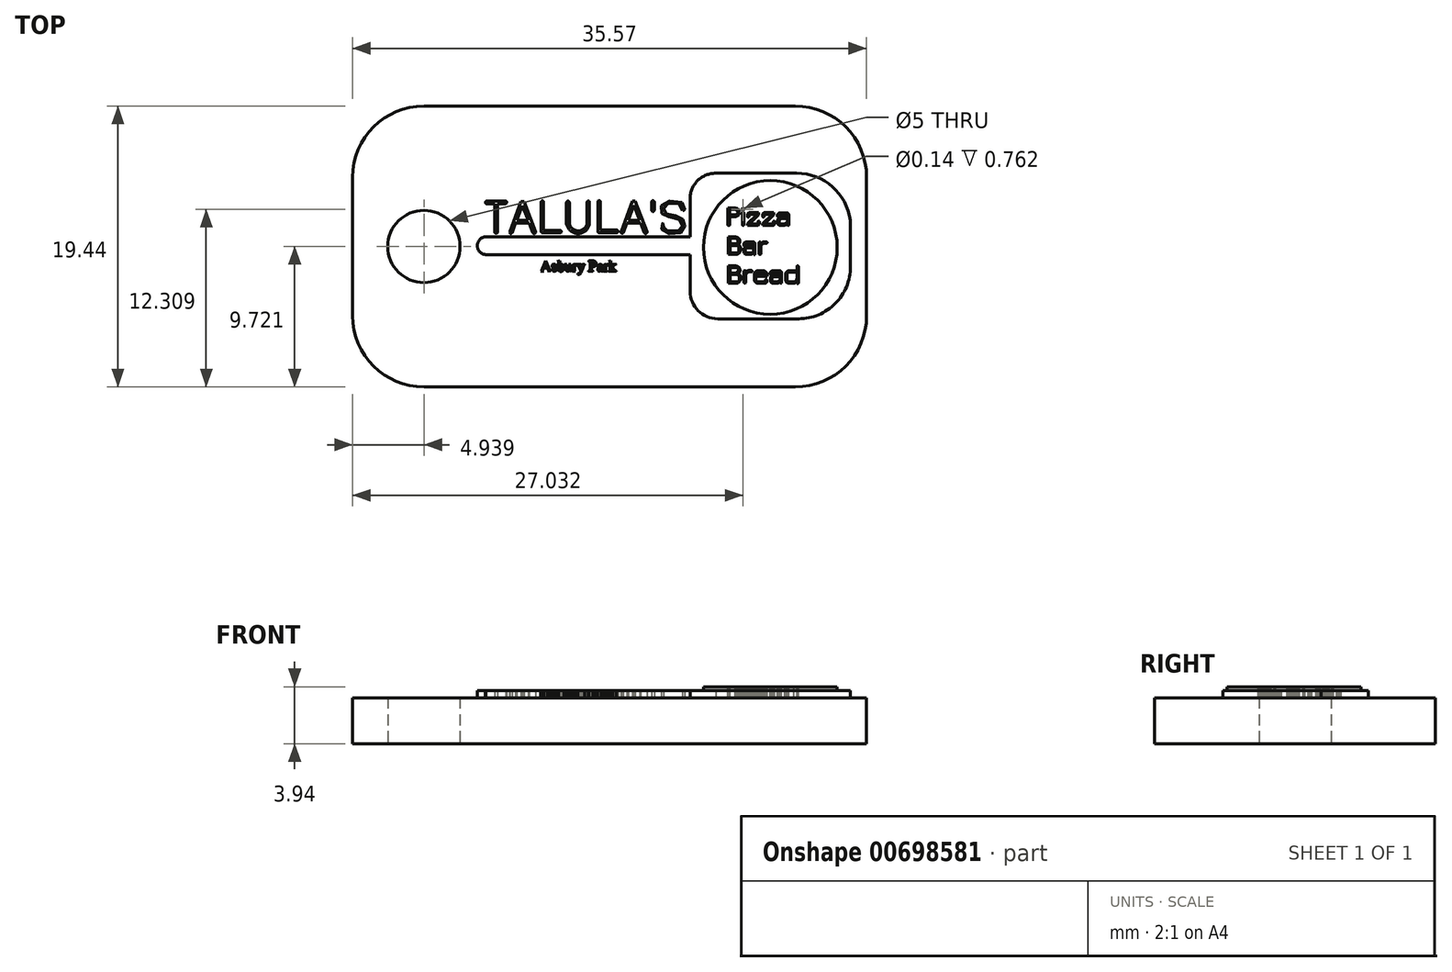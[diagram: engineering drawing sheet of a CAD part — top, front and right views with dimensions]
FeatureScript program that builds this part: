
annotation { "Feature Type Name" : "Feature", "Feature Type Description" : "" }
export const myFeature = defineFeature(function(context is Context, id is Id, definition is map)
    precondition{}
    {
        {
            var Q0;
            Q0=qCreatedBy(makeId("Top.planeOp"),FACE);
            var sketch = newSketch(context, id + "F0", { "sketchPlane" : qUnion([Q0])});
            skLineSegment(sketch, "E0.bottom", {"start": v(-4.93, 0) * mm, "end": v(-30.63, 0) * mm});
            skLineSegment(sketch, "E0.top", {"start": v(-4.93, 19.44) * mm, "end": v(-30.63, 19.44) * mm});
            skLineSegment(sketch, "E0.left", {"start": v(0, 4.93) * mm, "end": v(0, 14.5) * mm});
            skLineSegment(sketch, "E0.right", {"start": v(-35.57, 4.93) * mm, "end": v(-35.57, 14.5) * mm});
            skPoint(sketch, "E1.visualSharp", {"position": v(-35.57, 0) * mm});
            skArc(sketch, "E1.filletArc", {"start": v(-35.57, 4.93) * mm, "mid": v(-34.12, 1.45) * mm, "end": v(-30.63, 0) * mm});
            skPoint(sketch, "E2.visualSharp", {"position": v(-35.57, 19.44) * mm});
            skArc(sketch, "E2.filletArc", {"start": v(-30.63, 19.44) * mm, "mid": v(-34.12, 18) * mm, "end": v(-35.57, 14.5) * mm});
            skPoint(sketch, "E3.visualSharp", {"position": v(0, 19.44) * mm});
            skArc(sketch, "E3.filletArc", {"start": v(0, 14.5) * mm, "mid": v(-1.45, 18) * mm, "end": v(-4.93, 19.44) * mm});
            skPoint(sketch, "E4.visualSharp", {"position": v(0, 0) * mm});
            skArc(sketch, "E4.filletArc", {"start": v(-4.93, 0) * mm, "mid": v(-1.45, 1.45) * mm, "end": v(0, 4.93) * mm});
            skCircle(sketch, "E5", {"center": v(-30.63, 9.72) * mm, "radius": 2.5 * mm});
            skPoint(sketch, "E5.centerSnap0", {"position": v(-35.57, 9.72) * mm});
            skSolve(sketch);
        }
        {
            var Q0;
            Q0 = qSketchRegion(id + "F0", true);
            extrude(context, id + "F1", {"entities" : qUnion([Q0]), "depth" : 3.17 * mm, "offsetDistance" : 25.4 * mm});
        }
        {
            var Q0;
            Q0=makeQuery(id+"F1.opExtrude","CAP_FACE",FACE,{"disambiguationData":[OSD([sQuery(id+"F0.wireOp",EDGE,"E0.bottom"),sQuery(id+"F0.wireOp",EDGE,"E0.top"),sQuery(id+"F0.wireOp",EDGE,"E0.left"),sQuery(id+"F0.wireOp",EDGE,"E0.right"),sQuery(id+"F0.wireOp",EDGE,"E1.filletArc"),sQuery(id+"F0.wireOp",EDGE,"E2.filletArc"),sQuery(id+"F0.wireOp",EDGE,"E3.filletArc"),sQuery(id+"F0.wireOp",EDGE,"E4.filletArc"),sQuery(id+"F0.wireOp",EDGE,"E5")])],"isStart":false});
            var sketch = newSketch(context, id + "F2", { "sketchPlane" : qUnion([Q0])});
            skLineSegment(sketch, "E6", {"start": v(-26.47, 10.38) * mm, "end": v(-12.21, 10.38) * mm});
            skLineSegment(sketch, "E7", {"start": v(-12.21, 10.38) * mm, "end": v(-12.21, 13.03) * mm});
            skLineSegment(sketch, "E8", {"start": v(-10.42, 14.8) * mm, "end": v(-4.84, 14.8) * mm});
            skLineSegment(sketch, "E9", {"start": v(-1.12, 11.52) * mm, "end": v(-1.12, 8.32) * mm});
            skLineSegment(sketch, "E10", {"start": v(-10.3, 4.72) * mm, "end": v(-4.7, 4.72) * mm});
            skLineSegment(sketch, "E11", {"start": v(-26.37, 9.16) * mm, "end": v(-12.21, 9.16) * mm});
            skLineSegment(sketch, "E12", {"start": v(-12.21, 9.16) * mm, "end": v(-12.21, 6.63) * mm});
            skArc(sketch, "E13", {"start": v(-10.42, 14.8) * mm, "mid": v(-11.69, 14.28) * mm, "end": v(-12.21, 13.03) * mm});
            skArc(sketch, "E14", {"start": v(-1.12, 11.52) * mm, "mid": v(-2.37, 13.86) * mm, "end": v(-4.84, 14.8) * mm});
            skArc(sketch, "E15", {"start": v(-4.7, 4.72) * mm, "mid": v(-2.16, 5.78) * mm, "end": v(-1.12, 8.32) * mm});
            skArc(sketch, "E16", {"start": v(-12.21, 6.63) * mm, "mid": v(-11.65, 5.28) * mm, "end": v(-10.3, 4.72) * mm});
            skArc(sketch, "E17", {"start": v(-26.47, 10.38) * mm, "mid": v(-26.94, 9.73) * mm, "end": v(-26.37, 9.16) * mm});
            skLineSegment(sketch, "E18", {"start": v(-26.3, 12.86) * mm, "end": v(-24.96, 12.86) * mm});
            skLineSegment(sketch, "E19", {"start": v(-26.3, 12.69) * mm, "end": v(-25.72, 12.69) * mm});
            skLineSegment(sketch, "E20", {"start": v(-25.72, 12.69) * mm, "end": v(-25.72, 10.7) * mm});
            skLineSegment(sketch, "E21", {"start": v(-25.53, 10.7) * mm, "end": v(-25.53, 12.69) * mm});
            skLineSegment(sketch, "E22", {"start": v(-25.53, 12.69) * mm, "end": v(-24.96, 12.69) * mm});
            skArc(sketch, "E23", {"start": v(-24.96, 12.69) * mm, "mid": v(-24.9, 12.78) * mm, "end": v(-24.96, 12.86) * mm});
            skArc(sketch, "E24", {"start": v(-26.3, 12.86) * mm, "mid": v(-26.38, 12.78) * mm, "end": v(-26.3, 12.69) * mm});
            skArc(sketch, "E25", {"start": v(-25.72, 10.7) * mm, "mid": v(-25.63, 10.63) * mm, "end": v(-25.53, 10.7) * mm});
            skLineSegment(sketch, "E26", {"start": v(-24.69, 10.75) * mm, "end": v(-23.92, 12.85) * mm});
            skLineSegment(sketch, "E27", {"start": v(-23.92, 12.85) * mm, "end": v(-23.7, 12.85) * mm});
            skLineSegment(sketch, "E28", {"start": v(-23.7, 12.85) * mm, "end": v(-22.9, 10.74) * mm});
            skLineSegment(sketch, "E29", {"start": v(-24.2, 11.53) * mm, "end": v(-23.82, 12.56) * mm});
            skLineSegment(sketch, "E30", {"start": v(-23.82, 12.56) * mm, "end": v(-23.4, 11.53) * mm});
            skLineSegment(sketch, "E31", {"start": v(-23.4, 11.53) * mm, "end": v(-24.2, 11.53) * mm});
            skLineSegment(sketch, "E32", {"start": v(-24.53, 10.68) * mm, "end": v(-24.3, 11.34) * mm});
            skLineSegment(sketch, "E33", {"start": v(-24.3, 11.34) * mm, "end": v(-23.35, 11.34) * mm});
            skLineSegment(sketch, "E34", {"start": v(-23.35, 11.34) * mm, "end": v(-23.1, 10.68) * mm});
            skArc(sketch, "E35", {"start": v(-24.69, 10.75) * mm, "mid": v(-24.65, 10.63) * mm, "end": v(-24.53, 10.68) * mm});
            skArc(sketch, "E36", {"start": v(-23.1, 10.68) * mm, "mid": v(-22.97, 10.62) * mm, "end": v(-22.9, 10.74) * mm});
            skLineSegment(sketch, "E37", {"start": v(-22.5, 12.84) * mm, "end": v(-22.5, 10.75) * mm});
            skLineSegment(sketch, "E38", {"start": v(-22.36, 12.84) * mm, "end": v(-22.36, 10.84) * mm});
            skLineSegment(sketch, "E39", {"start": v(-22.36, 10.84) * mm, "end": v(-21.2, 10.84) * mm});
            skLineSegment(sketch, "E40", {"start": v(-22.44, 10.66) * mm, "end": v(-21.2, 10.66) * mm});
            skArc(sketch, "E41", {"start": v(-22.36, 12.84) * mm, "mid": v(-22.43, 12.88) * mm, "end": v(-22.5, 12.84) * mm});
            skArc(sketch, "E42", {"start": v(-22.5, 10.75) * mm, "mid": v(-22.49, 10.7) * mm, "end": v(-22.44, 10.66) * mm});
            skArc(sketch, "E43", {"start": v(-21.2, 10.66) * mm, "mid": v(-21.12, 10.75) * mm, "end": v(-21.2, 10.84) * mm});
            skLineSegment(sketch, "E44", {"start": v(-18.59, 12.86) * mm, "end": v(-18.59, 10.77) * mm});
            skLineSegment(sketch, "E45", {"start": v(-18.44, 12.86) * mm, "end": v(-18.44, 10.86) * mm});
            skLineSegment(sketch, "E46", {"start": v(-18.44, 10.86) * mm, "end": v(-17.29, 10.86) * mm});
            skLineSegment(sketch, "E47", {"start": v(-18.52, 10.68) * mm, "end": v(-17.28, 10.68) * mm});
            skArc(sketch, "E48", {"start": v(-18.44, 12.86) * mm, "mid": v(-18.51, 12.9) * mm, "end": v(-18.59, 12.86) * mm});
            skArc(sketch, "E49", {"start": v(-18.59, 10.77) * mm, "mid": v(-18.57, 10.72) * mm, "end": v(-18.52, 10.68) * mm});
            skArc(sketch, "E50", {"start": v(-17.28, 10.68) * mm, "mid": v(-17.2, 10.77) * mm, "end": v(-17.29, 10.86) * mm});
            skLineSegment(sketch, "E51", {"start": v(-16.98, 10.76) * mm, "end": v(-16.2, 12.86) * mm});
            skLineSegment(sketch, "E52", {"start": v(-16.2, 12.86) * mm, "end": v(-16, 12.86) * mm});
            skLineSegment(sketch, "E53", {"start": v(-16, 12.86) * mm, "end": v(-15.2, 10.74) * mm});
            skLineSegment(sketch, "E54", {"start": v(-16.5, 11.54) * mm, "end": v(-16.1, 12.57) * mm});
            skLineSegment(sketch, "E55", {"start": v(-16.1, 12.57) * mm, "end": v(-15.7, 11.54) * mm});
            skLineSegment(sketch, "E56", {"start": v(-15.7, 11.54) * mm, "end": v(-16.5, 11.54) * mm});
            skLineSegment(sketch, "E57", {"start": v(-16.82, 10.69) * mm, "end": v(-16.58, 11.34) * mm});
            skLineSegment(sketch, "E58", {"start": v(-16.58, 11.34) * mm, "end": v(-15.64, 11.34) * mm});
            skLineSegment(sketch, "E59", {"start": v(-15.64, 11.34) * mm, "end": v(-15.39, 10.68) * mm});
            skArc(sketch, "E60", {"start": v(-16.98, 10.76) * mm, "mid": v(-16.94, 10.64) * mm, "end": v(-16.82, 10.69) * mm});
            skArc(sketch, "E61", {"start": v(-15.39, 10.68) * mm, "mid": v(-15.26, 10.63) * mm, "end": v(-15.2, 10.74) * mm});
            skArc(sketch, "E62", {"start": v(-20.57, 11.3) * mm, "mid": v(-19.95, 10.8) * mm, "end": v(-19.34, 11.3) * mm});
            skArc(sketch, "E63", {"start": v(-20.76, 11.28) * mm, "mid": v(-19.96, 10.62) * mm, "end": v(-19.17, 11.3) * mm});
            skLineSegment(sketch, "E64", {"start": v(-20.76, 11.28) * mm, "end": v(-20.76, 12.77) * mm});
            skLineSegment(sketch, "E65", {"start": v(-20.57, 11.3) * mm, "end": v(-20.57, 12.77) * mm});
            skLineSegment(sketch, "E66", {"start": v(-19.34, 11.3) * mm, "end": v(-19.34, 12.77) * mm});
            skLineSegment(sketch, "E67", {"start": v(-19.17, 11.3) * mm, "end": v(-19.17, 12.79) * mm});
            skArc(sketch, "E68", {"start": v(-20.57, 12.77) * mm, "mid": v(-20.67, 12.87) * mm, "end": v(-20.76, 12.77) * mm});
            skArc(sketch, "E69", {"start": v(-19.17, 12.79) * mm, "mid": v(-19.26, 12.87) * mm, "end": v(-19.34, 12.77) * mm});
            skLineSegment(sketch, "E70", {"start": v(-14.86, 12.22) * mm, "end": v(-14.86, 12.81) * mm});
            skLineSegment(sketch, "E71", {"start": v(-14.7, 12.22) * mm, "end": v(-14.7, 12.83) * mm});
            skArc(sketch, "E72", {"start": v(-14.7, 12.83) * mm, "mid": v(-14.79, 12.9) * mm, "end": v(-14.86, 12.81) * mm});
            skArc(sketch, "E73", {"start": v(-14.86, 12.22) * mm, "mid": v(-14.78, 12.14) * mm, "end": v(-14.7, 12.22) * mm});
            skFitSpline(sketch, "E74", {"points": [v(-12.75, 12.2) * mm, v(-12.78, 12.43) * mm, v(-12.8, 12.53) * mm, v(-12.91, 12.63) * mm, v(-13.07, 12.7) * mm, v(-13.36, 12.72) * mm, v(-13.78, 12.71) * mm, v(-13.9, 12.64) * mm, v(-14, 12.53) * mm, v(-14.03, 12.43) * mm, v(-14.04, 12.22) * mm, v(-14, 12.12) * mm, v(-13.98, 12.07) * mm, v(-13.92, 12.01) * mm, v(-13.84, 11.98) * mm, v(-13.78, 11.96) * mm, v(-13.58, 11.92) * mm, v(-13.16, 11.83) * mm, v(-12.97, 11.79) * mm, v(-12.84, 11.72) * mm, v(-12.73, 11.62) * mm, v(-12.66, 11.52) * mm, v(-12.62, 11.44) * mm, v(-12.6, 11.38) * mm, v(-12.58, 11.16) * mm, v(-12.61, 10.99) * mm, v(-12.7, 10.82) * mm, v(-12.81, 10.72) * mm, v(-12.99, 10.64) * mm, v(-13.35, 10.62) * mm, v(-13.76, 10.63) * mm, v(-13.93, 10.69) * mm, v(-14.12, 10.83) * mm, v(-14.18, 10.98) * mm, v(-14.2, 11.14) * mm, v(-14.2, 11.31) * mm, v(-14.14, 11.34) * mm, v(-14.1, 11.34) * mm, v(-14.08, 11.33) * mm, v(-14.07, 11.3) * mm, v(-14.06, 11.25) * mm, v(-14.06, 11.17) * mm, v(-14.05, 11.08) * mm, v(-14.04, 11.01) * mm, v(-14.02, 10.97) * mm, v(-13.98, 10.92) * mm, v(-13.95, 10.87) * mm, v(-13.88, 10.84) * mm, v(-13.78, 10.83) * mm, v(-13.32, 10.8) * mm, v(-13.03, 10.81) * mm, v(-12.88, 10.88) * mm, v(-12.84, 10.94) * mm, v(-12.78, 11.04) * mm, v(-12.76, 11.15) * mm, v(-12.77, 11.35) * mm, v(-12.82, 11.47) * mm, v(-12.9, 11.55) * mm, v(-13.06, 11.62) * mm, v(-13.3, 11.67) * mm, v(-13.7, 11.77) * mm, v(-13.95, 11.83) * mm, v(-14.05, 11.87) * mm, v(-14.15, 11.98) * mm, v(-14.17, 12.03) * mm, v(-14.2, 12.07) * mm, v(-14.2, 12.17) * mm, v(-14.2, 12.43) * mm, v(-14.13, 12.65) * mm, v(-13.94, 12.83) * mm, v(-13.71, 12.86) * mm, v(-13.04, 12.86) * mm, v(-12.82, 12.8) * mm, v(-12.71, 12.72) * mm, v(-12.64, 12.6) * mm, v(-12.6, 12.48) * mm, v(-12.58, 12.28) * mm, v(-12.59, 12.24) * mm, v(-12.61, 12.17) * mm, v(-12.63, 12.16) * mm, v(-12.67, 12.16) * mm, v(-12.72, 12.16) * mm, v(-12.75, 12.2) * mm]});
            skPoint(sketch, "E75.1.internal.orphan", {"position": v(-13.07, 12.73) * mm});
            skCircle(sketch, "E76", {"center": v(-6.66, 9.66) * mm, "radius": 4.63 * mm});
            skPoint(sketch, "E76.perimeterSnap0", {"position": v(-6.66, 9.66) * mm});
            skPoint(sketch, "E76.perimeterSnap1", {"position": v(-11.69, 14.28) * mm});
            skLineSegment(sketch, "E77", {"start": v(-22.48, 8.07) * mm, "end": v(-22.2, 8.73) * mm});
            skLineSegment(sketch, "E78", {"start": v(-22.2, 8.73) * mm, "end": v(-21.92, 8.07) * mm});
            skLineSegment(sketch, "E79", {"start": v(-22.48, 8.07) * mm, "end": v(-22.5, 8.04) * mm});
            skLineSegment(sketch, "E80", {"start": v(-22.5, 8.04) * mm, "end": v(-22.54, 8.02) * mm});
            skLineSegment(sketch, "E81", {"start": v(-22.54, 8.02) * mm, "end": v(-22.34, 8.02) * mm});
            skLineSegment(sketch, "E82", {"start": v(-22.34, 8.02) * mm, "end": v(-22.38, 8.03) * mm});
            skLineSegment(sketch, "E83", {"start": v(-22.38, 8.03) * mm, "end": v(-22.43, 8.06) * mm});
            skLineSegment(sketch, "E84", {"start": v(-22.43, 8.06) * mm, "end": v(-22.35, 8.23) * mm});
            skLineSegment(sketch, "E85", {"start": v(-22.35, 8.23) * mm, "end": v(-22.07, 8.23) * mm});
            skLineSegment(sketch, "E86", {"start": v(-22.07, 8.23) * mm, "end": v(-22, 8.07) * mm});
            skLineSegment(sketch, "E87", {"start": v(-22, 8.07) * mm, "end": v(-22.04, 8.04) * mm});
            skLineSegment(sketch, "E88", {"start": v(-22.04, 8.04) * mm, "end": v(-22.09, 8.03) * mm});
            skLineSegment(sketch, "E89", {"start": v(-22.09, 8.03) * mm, "end": v(-21.84, 8.03) * mm});
            skLineSegment(sketch, "E90", {"start": v(-21.84, 8.03) * mm, "end": v(-21.92, 8.07) * mm});
            skLineSegment(sketch, "E91", {"start": v(-22.21, 8.56) * mm, "end": v(-22.34, 8.26) * mm});
            skLineSegment(sketch, "E92", {"start": v(-22.34, 8.26) * mm, "end": v(-22.1, 8.26) * mm});
            skLineSegment(sketch, "E93", {"start": v(-22.1, 8.26) * mm, "end": v(-22.21, 8.56) * mm});
            skLineSegment(sketch, "E94", {"start": v(-21.4, 8.69) * mm, "end": v(-21.24, 8.75) * mm});
            skLineSegment(sketch, "E95", {"start": v(-21.24, 8.75) * mm, "end": v(-21.24, 8.43) * mm});
            skLineSegment(sketch, "E96", {"start": v(-21.4, 8.69) * mm, "end": v(-21.33, 8.69) * mm});
            skLineSegment(sketch, "E97", {"start": v(-21.33, 8.69) * mm, "end": v(-21.33, 8.07) * mm});
            skLineSegment(sketch, "E98", {"start": v(-21.23, 8.38) * mm, "end": v(-21.23, 8.08) * mm});
            skLineSegment(sketch, "E99", {"start": v(-21, 8.35) * mm, "end": v(-21, 8.16) * mm});
            skLineSegment(sketch, "E100", {"start": v(-20.92, 8.35) * mm, "end": v(-20.92, 8.18) * mm});
            skLineSegment(sketch, "E101", {"start": v(-20.74, 8.12) * mm, "end": v(-20.74, 8.48) * mm});
            skLineSegment(sketch, "E102", {"start": v(-20.74, 8.48) * mm, "end": v(-20.9, 8.48) * mm});
            skLineSegment(sketch, "E103", {"start": v(-20.9, 8.48) * mm, "end": v(-20.87, 8.46) * mm});
            skLineSegment(sketch, "E104", {"start": v(-20.87, 8.46) * mm, "end": v(-20.8, 8.46) * mm});
            skLineSegment(sketch, "E105", {"start": v(-20.8, 8.46) * mm, "end": v(-20.8, 8.1) * mm});
            skLineSegment(sketch, "E106", {"start": v(-20.72, 8.01) * mm, "end": v(-20.65, 8.01) * mm});
            skLineSegment(sketch, "E107", {"start": v(-20.52, 8.08) * mm, "end": v(-20.52, 8) * mm});
            skLineSegment(sketch, "E108", {"start": v(-20.52, 8) * mm, "end": v(-20.4, 8.08) * mm});
            skLineSegment(sketch, "E109", {"start": v(-20.4, 8.08) * mm, "end": v(-20.45, 8.08) * mm});
            skLineSegment(sketch, "E110", {"start": v(-20.45, 8.08) * mm, "end": v(-20.45, 8.5) * mm});
            skLineSegment(sketch, "E111", {"start": v(-20.45, 8.5) * mm, "end": v(-20.6, 8.5) * mm});
            skLineSegment(sketch, "E112", {"start": v(-20.6, 8.5) * mm, "end": v(-20.6, 8.46) * mm});
            skLineSegment(sketch, "E113", {"start": v(-20.6, 8.46) * mm, "end": v(-20.53, 8.46) * mm});
            skLineSegment(sketch, "E114", {"start": v(-20.53, 8.46) * mm, "end": v(-20.53, 8.13) * mm});
            skLineSegment(sketch, "E115", {"start": v(-21.47, 8.48) * mm, "end": v(-21.47, 8.36) * mm});
            skLineSegment(sketch, "E116", {"start": v(-21.76, 8.16) * mm, "end": v(-21.76, 8) * mm});
            skLineSegment(sketch, "E117", {"start": v(-21.64, 8) * mm, "end": v(-21.57, 8) * mm});
            skLineSegment(sketch, "E118", {"start": v(-20.36, 8.42) * mm, "end": v(-20.3, 8.42) * mm});
            skLineSegment(sketch, "E119", {"start": v(-20.3, 8.42) * mm, "end": v(-20.3, 8.06) * mm});
            skLineSegment(sketch, "E120", {"start": v(-20.2, 8.5) * mm, "end": v(-20.2, 8.44) * mm});
            skLineSegment(sketch, "E121", {"start": v(-20.2, 8.39) * mm, "end": v(-20.2, 8.07) * mm});
            skLineSegment(sketch, "E122", {"start": v(-20.35, 8.01) * mm, "end": v(-20.13, 8.01) * mm});
            skLineSegment(sketch, "E123", {"start": v(-20.02, 8.5) * mm, "end": v(-19.82, 8.5) * mm});
            skLineSegment(sketch, "E124", {"start": v(-19.65, 8.5) * mm, "end": v(-19.5, 8.5) * mm});
            skLineSegment(sketch, "E125", {"start": v(-19.97, 8.46) * mm, "end": v(-19.77, 8.03) * mm});
            skLineSegment(sketch, "E126", {"start": v(-19.87, 8.41) * mm, "end": v(-19.74, 8.13) * mm});
            skLineSegment(sketch, "E127", {"start": v(-19.74, 8.13) * mm, "end": v(-19.61, 8.42) * mm});
            skPoint(sketch, "E128.10.internal.snap0", {"position": v(-21.62, 8.5) * mm});
            skFitSpline(sketch, "E128", {"points": [v(-21.47, 8.48) * mm, v(-21.51, 8.47) * mm, v(-21.55, 8.48) * mm, v(-21.58, 8.5) * mm, v(-21.65, 8.5) * mm, v(-21.7, 8.48) * mm, v(-21.75, 8.43) * mm, v(-21.77, 8.37) * mm, v(-21.76, 8.32) * mm, v(-21.73, 8.28) * mm, v(-21.62, 8.2) * mm, v(-21.54, 8.17) * mm, v(-21.52, 8.14) * mm, v(-21.52, 8.1) * mm, v(-21.56, 8.05) * mm, v(-21.63, 8.04) * mm, v(-21.68, 8.08) * mm, v(-21.73, 8.15) * mm, v(-21.76, 8.16) * mm], "startDerivative": vector(-0.78, -0.39) * mm, "endDerivative": vector(-0.74, 0.12) * mm});
            skFitSpline(sketch, "E129", {"points": [v(-21.76, 8) * mm, v(-21.72, 8.04) * mm, v(-21.68, 8.02) * mm, v(-21.64, 8) * mm, v(-21.57, 8) * mm, v(-21.5, 8.02) * mm, v(-21.45, 8.08) * mm, v(-21.43, 8.14) * mm, v(-21.47, 8.22) * mm, v(-21.58, 8.3) * mm, v(-21.64, 8.32) * mm, v(-21.69, 8.36) * mm, v(-21.7, 8.42) * mm, v(-21.63, 8.46) * mm, v(-21.56, 8.44) * mm, v(-21.52, 8.4) * mm, v(-21.51, 8.36) * mm, v(-21.47, 8.33) * mm, v(-21.47, 8.36) * mm], "startDerivative": vector(0.84, 1.07) * mm, "endDerivative": vector(-0.22, 0.9) * mm});
            skFitSpline(sketch, "E130", {"points": [v(-21.23, 8.08) * mm, v(-21.15, 8.04) * mm, v(-21.05, 8.08) * mm, v(-21, 8.16) * mm], "startDerivative": vector(0.25, -0.16) * mm, "endDerivative": vector(0.1, 0.3) * mm});
            skFitSpline(sketch, "E131", {"points": [v(-21.23, 8.38) * mm, v(-21.15, 8.44) * mm, v(-21.07, 8.43) * mm, v(-21, 8.35) * mm], "startDerivative": vector(0.25, 0.21) * mm, "endDerivative": vector(0.16, -0.27) * mm});
            skFitSpline(sketch, "E132", {"points": [v(-21.24, 8.43) * mm, v(-21.15, 8.5) * mm, v(-21.04, 8.48) * mm, v(-20.92, 8.35) * mm], "startDerivative": vector(0.26, 0.25) * mm, "endDerivative": vector(0.26, -0.43) * mm});
            skFitSpline(sketch, "E133", {"points": [v(-20.92, 8.18) * mm, v(-21, 8.06) * mm, v(-21.12, 8) * mm, v(-21.23, 8) * mm, v(-21.33, 8.07) * mm], "startDerivative": vector(-0.22, -0.47) * mm, "endDerivative": vector(-0.4, 0.33) * mm});
            skFitSpline(sketch, "E134", {"points": [v(-20.74, 8.12) * mm, v(-20.67, 8.05) * mm, v(-20.53, 8.13) * mm], "startDerivative": vector(0.12, -0.21) * mm, "endDerivative": vector(0.29, 0.22) * mm});
            skFitSpline(sketch, "E135", {"points": [v(-20.8, 8.1) * mm, v(-20.77, 8.04) * mm, v(-20.72, 8.01) * mm], "startDerivative": vector(0.03, -0.16) * mm, "endDerivative": vector(0.13, -0.04) * mm});
            skFitSpline(sketch, "E136", {"points": [v(-20.65, 8.01) * mm, v(-20.59, 8.03) * mm, v(-20.52, 8.08) * mm], "startDerivative": vector(0.13, 0.04) * mm, "endDerivative": vector(0.14, 0.1) * mm});
            skFitSpline(sketch, "E137", {"points": [v(-20.36, 8.42) * mm, v(-20.31, 8.46) * mm, v(-20.2, 8.5) * mm], "startDerivative": vector(0.1, 0.1) * mm, "endDerivative": vector(0.22, 0.05) * mm});
            skFitSpline(sketch, "E138", {"points": [v(-20.3, 8.06) * mm, v(-20.3, 8.04) * mm, v(-20.32, 8.03) * mm, v(-20.35, 8.01) * mm], "startDerivative": vector(-0.05, -0.08) * mm, "endDerivative": vector(-0.08, -0.05) * mm});
            skFitSpline(sketch, "E139", {"points": [v(-20.2, 8.07) * mm, v(-20.2, 8.05) * mm, v(-20.13, 8.01) * mm], "startDerivative": vector(-0.02, -0.05) * mm, "endDerivative": vector(0.12, -0.05) * mm});
            skFitSpline(sketch, "E140", {"points": [v(-20.2, 8.44) * mm, v(-20.13, 8.5) * mm, v(-20.06, 8.49) * mm, v(-20.03, 8.46) * mm, v(-20.05, 8.43) * mm, v(-20.08, 8.42) * mm, v(-20.1, 8.44) * mm, v(-20.1, 8.44) * mm, v(-20.15, 8.43) * mm, v(-20.2, 8.39) * mm], "startDerivative": vector(0.39, 0.46) * mm, "endDerivative": vector(-0.3, -0.36) * mm});
            skFitSpline(sketch, "E141", {"points": [v(-20.02, 8.5) * mm, v(-20.02, 8.47) * mm, v(-19.97, 8.46) * mm], "startDerivative": vector(-0.02, -0.06) * mm, "endDerivative": vector(0.1, -0.02) * mm});
            skFitSpline(sketch, "E142", {"points": [v(-19.82, 8.5) * mm, v(-19.79, 8.49) * mm, v(-19.83, 8.47) * mm, v(-19.85, 8.46) * mm, v(-19.87, 8.44) * mm, v(-19.87, 8.41) * mm], "startDerivative": vector(0.23, -0.03) * mm, "endDerivative": vector(0.06, -0.17) * mm});
            skPoint(sketch, "E143.2.internal.snap0", {"position": v(-19.67, 8.28) * mm});
            skFitSpline(sketch, "E143", {"points": [v(-19.65, 8.5) * mm, v(-19.67, 8.48) * mm, v(-19.67, 8.48) * mm, v(-19.67, 8.47) * mm, v(-19.66, 8.46) * mm, v(-19.65, 8.46) * mm, v(-19.63, 8.46) * mm, v(-19.62, 8.46) * mm, v(-19.6, 8.46) * mm, v(-19.6, 8.44) * mm, v(-19.61, 8.42) * mm], "startDerivative": vector(-0.14, -0.08) * mm, "endDerivative": vector(0.04, -0.18) * mm});
            skFitSpline(sketch, "E144", {"points": [v(-19.77, 8.03) * mm, v(-19.8, 7.93) * mm, v(-19.85, 7.84) * mm, v(-19.88, 7.84) * mm, v(-19.9, 7.84) * mm, v(-19.92, 7.86) * mm, v(-19.94, 7.86) * mm, v(-19.97, 7.85) * mm, v(-20, 7.84) * mm, v(-20, 7.8) * mm, v(-19.98, 7.8) * mm, v(-19.95, 7.78) * mm, v(-19.9, 7.78) * mm, v(-19.87, 7.79) * mm, v(-19.86, 7.8) * mm, v(-19.83, 7.81) * mm, v(-19.73, 7.97) * mm, v(-19.62, 8.26) * mm, v(-19.57, 8.4) * mm, v(-19.56, 8.44) * mm, v(-19.53, 8.46) * mm, v(-19.5, 8.47) * mm, v(-19.5, 8.48) * mm, v(-19.5, 8.5) * mm, v(-19.5, 8.5) * mm], "startDerivative": vector(-0.53, -1.52) * mm, "endDerivative": vector(-0.83, -0.18) * mm});
            skLineSegment(sketch, "E145", {"start": v(-19.13, 8.66) * mm, "end": v(-19.13, 8.07) * mm});
            skLineSegment(sketch, "E146", {"start": v(-19.03, 8.68) * mm, "end": v(-19.03, 8.37) * mm});
            skLineSegment(sketch, "E147", {"start": v(-19.03, 8.37) * mm, "end": v(-18.91, 8.37) * mm});
            skLineSegment(sketch, "E148", {"start": v(-19.04, 8.1) * mm, "end": v(-19.04, 8.34) * mm});
            skLineSegment(sketch, "E149", {"start": v(-19.04, 8.34) * mm, "end": v(-18.88, 8.34) * mm});
            skLineSegment(sketch, "E150", {"start": v(-19.22, 8) * mm, "end": v(-18.93, 8) * mm});
            skLineSegment(sketch, "E151", {"start": v(-18.37, 8.42) * mm, "end": v(-18.37, 8.4) * mm});
            skLineSegment(sketch, "E152", {"start": v(-18.37, 8.4) * mm, "end": v(-18.37, 8.32) * mm});
            skLineSegment(sketch, "E153", {"start": v(-18.36, 8.28) * mm, "end": v(-18.36, 8.12) * mm});
            skLineSegment(sketch, "E154", {"start": v(-18.3, 8.42) * mm, "end": v(-18.3, 8.11) * mm});
            skLineSegment(sketch, "E155", {"start": v(-19.22, 8.72) * mm, "end": v(-18.88, 8.72) * mm});
            skLineSegment(sketch, "E156", {"start": v(-18.12, 8.42) * mm, "end": v(-18.12, 8.08) * mm});
            skLineSegment(sketch, "E157", {"start": v(-18.04, 8.48) * mm, "end": v(-18.04, 8.43) * mm});
            skLineSegment(sketch, "E158", {"start": v(-18.04, 8.38) * mm, "end": v(-18.04, 8.08) * mm});
            skLineSegment(sketch, "E159", {"start": v(-18.19, 8.01) * mm, "end": v(-17.97, 8.01) * mm});
            skLineSegment(sketch, "E160", {"start": v(-17.84, 8.01) * mm, "end": v(-17.61, 8.01) * mm});
            skLineSegment(sketch, "E161", {"start": v(-17.56, 8) * mm, "end": v(-17.33, 8) * mm});
            skLineSegment(sketch, "E162", {"start": v(-17.4, 8.06) * mm, "end": v(-17.6, 8.29) * mm});
            skLineSegment(sketch, "E163", {"start": v(-17.6, 8.29) * mm, "end": v(-17.44, 8.45) * mm});
            skLineSegment(sketch, "E164", {"start": v(-17.7, 8.06) * mm, "end": v(-17.7, 8.26) * mm});
            skLineSegment(sketch, "E165", {"start": v(-17.7, 8.26) * mm, "end": v(-17.67, 8.26) * mm});
            skLineSegment(sketch, "E166", {"start": v(-17.67, 8.26) * mm, "end": v(-17.5, 8.05) * mm});
            skLineSegment(sketch, "E167", {"start": v(-17.68, 8.75) * mm, "end": v(-17.68, 8.3) * mm});
            skLineSegment(sketch, "E168", {"start": v(-17.68, 8.3) * mm, "end": v(-17.52, 8.44) * mm});
            skLineSegment(sketch, "E169", {"start": v(-17.55, 8.5) * mm, "end": v(-17.35, 8.5) * mm});
            skLineSegment(sketch, "E170", {"start": v(-17.76, 8.67) * mm, "end": v(-17.76, 8.07) * mm});
            skLineSegment(sketch, "E171", {"start": v(-17.84, 8.69) * mm, "end": v(-17.68, 8.75) * mm});
            skLineSegment(sketch, "E172", {"start": v(-17.84, 8.69) * mm, "end": v(-17.76, 8.67) * mm});
            skFitSpline(sketch, "E173", {"points": [v(-19.22, 8.72) * mm, v(-19.23, 8.72) * mm, v(-19.23, 8.71) * mm, v(-19.23, 8.7) * mm, v(-19.23, 8.7) * mm, v(-19.2, 8.69) * mm, v(-19.2, 8.69) * mm, v(-19.18, 8.69) * mm, v(-19.16, 8.69) * mm, v(-19.15, 8.68) * mm, v(-19.14, 8.67) * mm, v(-19.13, 8.66) * mm], "startDerivative": vector(-0.1, -0.1) * mm, "endDerivative": vector(0.03, -0.13) * mm});
            skFitSpline(sketch, "E174", {"points": [v(-19.03, 8.68) * mm, v(-18.91, 8.68) * mm, v(-18.85, 8.64) * mm, v(-18.82, 8.59) * mm, v(-18.82, 8.54) * mm, v(-18.82, 8.52) * mm, v(-18.82, 8.46) * mm, v(-18.87, 8.4) * mm, v(-18.91, 8.37) * mm], "startDerivative": vector(0.73, 0.08) * mm, "endDerivative": vector(-0.37, -0.27) * mm});
            skFitSpline(sketch, "E175", {"points": [v(-18.88, 8.34) * mm, v(-18.8, 8.36) * mm, v(-18.75, 8.41) * mm, v(-18.72, 8.48) * mm, v(-18.72, 8.59) * mm, v(-18.73, 8.6) * mm, v(-18.74, 8.64) * mm, v(-18.77, 8.68) * mm, v(-18.88, 8.72) * mm], "startDerivative": vector(0.65, 0.13) * mm, "endDerivative": vector(-0.8, 0.26) * mm});
            skFitSpline(sketch, "E176", {"points": [v(-19.13, 8.07) * mm, v(-19.14, 8.05) * mm, v(-19.23, 8.04) * mm, v(-19.24, 8.03) * mm, v(-19.24, 8.02) * mm, v(-19.23, 8.01) * mm, v(-19.22, 8) * mm], "startDerivative": vector(0, -0.12) * mm, "endDerivative": vector(0.1, -0.03) * mm});
            skFitSpline(sketch, "E177", {"points": [v(-19.04, 8.1) * mm, v(-19.04, 8.07) * mm, v(-19.01, 8.04) * mm, v(-18.98, 8.04) * mm, v(-18.97, 8.04) * mm, v(-18.93, 8.03) * mm, v(-18.92, 8.02) * mm, v(-18.93, 8) * mm], "startDerivative": vector(0, -0.18) * mm, "endDerivative": vector(-0.14, -0.1) * mm});
            skFitSpline(sketch, "E178", {"points": [v(-18.37, 8.42) * mm, v(-18.38, 8.45) * mm, v(-18.44, 8.46) * mm, v(-18.5, 8.45) * mm, v(-18.53, 8.43) * mm, v(-18.53, 8.4) * mm, v(-18.53, 8.35) * mm, v(-18.55, 8.33) * mm, v(-18.57, 8.32) * mm, v(-18.59, 8.32) * mm, v(-18.6, 8.33) * mm, v(-18.6, 8.37) * mm, v(-18.6, 8.4) * mm, v(-18.57, 8.43) * mm, v(-18.53, 8.47) * mm, v(-18.49, 8.48) * mm, v(-18.4, 8.49) * mm, v(-18.35, 8.47) * mm, v(-18.31, 8.44) * mm, v(-18.3, 8.42) * mm], "startDerivative": vector(-0.2, 0.66) * mm, "endDerivative": vector(0.31, -0.48) * mm});
            skFitSpline(sketch, "E179", {"points": [v(-18.36, 8.28) * mm, v(-18.4, 8.28) * mm, v(-18.46, 8.24) * mm, v(-18.53, 8.19) * mm, v(-18.54, 8.14) * mm, v(-18.53, 8.11) * mm, v(-18.49, 8.08) * mm, v(-18.43, 8.09) * mm, v(-18.36, 8.12) * mm], "startDerivative": vector(-0.29, 0.05) * mm, "endDerivative": vector(0.45, 0.21) * mm});
            skFitSpline(sketch, "E180", {"points": [v(-18.37, 8.32) * mm, v(-18.4, 8.32) * mm, v(-18.47, 8.28) * mm, v(-18.6, 8.17) * mm, v(-18.6, 8.11) * mm, v(-18.58, 8.05) * mm, v(-18.53, 8.02) * mm, v(-18.48, 8.02) * mm, v(-18.42, 8.04) * mm, v(-18.4, 8.06) * mm, v(-18.38, 8.07) * mm, v(-18.37, 8.07) * mm, v(-18.36, 8.04) * mm, v(-18.35, 8.03) * mm, v(-18.3, 8.01) * mm, v(-18.25, 8.03) * mm, v(-18.2, 8.06) * mm, v(-18.2, 8.07) * mm, v(-18.2, 8.08) * mm, v(-18.2, 8.08) * mm, v(-18.22, 8.08) * mm, v(-18.25, 8.06) * mm, v(-18.26, 8.06) * mm, v(-18.28, 8.06) * mm, v(-18.3, 8.08) * mm, v(-18.3, 8.11) * mm], "startDerivative": vector(-0.93, 0.12) * mm, "endDerivative": vector(0.15, 0.98) * mm});
            skFitSpline(sketch, "E181", {"points": [v(-18.12, 8.08) * mm, v(-18.12, 8.06) * mm, v(-18.15, 8.03) * mm, v(-18.2, 8.03) * mm, v(-18.2, 8.02) * mm, v(-18.19, 8.01) * mm], "startDerivative": vector(0.02, -0.1) * mm, "endDerivative": vector(0.07, -0.06) * mm});
            skFitSpline(sketch, "E182", {"points": [v(-18.04, 8.08) * mm, v(-18.04, 8.07) * mm, v(-18.04, 8.06) * mm, v(-18.03, 8.05) * mm, v(-18, 8.04) * mm, v(-17.98, 8.04) * mm, v(-17.96, 8.04) * mm, v(-17.95, 8.02) * mm, v(-17.97, 8.01) * mm], "startDerivative": vector(0, -0.1) * mm, "endDerivative": vector(-0.12, -0.06) * mm});
            skFitSpline(sketch, "E183", {"points": [v(-18.04, 8.43) * mm, v(-18, 8.46) * mm, v(-17.96, 8.48) * mm, v(-17.9, 8.49) * mm, v(-17.87, 8.46) * mm, v(-17.87, 8.43) * mm, v(-17.9, 8.42) * mm, v(-17.92, 8.43) * mm, v(-17.92, 8.44) * mm, v(-17.94, 8.45) * mm, v(-17.98, 8.44) * mm, v(-18.04, 8.38) * mm], "startDerivative": vector(0.4, 0.35) * mm, "endDerivative": vector(-0.4, -0.55) * mm});
            skFitSpline(sketch, "E184", {"points": [v(-18.04, 8.48) * mm, v(-18.05, 8.49) * mm, v(-18.1, 8.48) * mm, v(-18.18, 8.43) * mm, v(-18.18, 8.42) * mm, v(-18.12, 8.42) * mm], "startDerivative": vector(-0.04, 0.13) * mm, "endDerivative": vector(0.3, 0.02) * mm});
            skFitSpline(sketch, "E185", {"points": [v(-17.84, 8.01) * mm, v(-17.85, 8.01) * mm, v(-17.86, 8.02) * mm, v(-17.86, 8.02) * mm, v(-17.85, 8.03) * mm, v(-17.82, 8.03) * mm, v(-17.79, 8.04) * mm, v(-17.77, 8.05) * mm, v(-17.76, 8.07) * mm], "startDerivative": vector(-0.13, 0) * mm, "endDerivative": vector(0, 0.15) * mm});
            skFitSpline(sketch, "E186", {"points": [v(-17.7, 8.06) * mm, v(-17.7, 8.05) * mm, v(-17.7, 8.05) * mm, v(-17.7, 8.04) * mm, v(-17.68, 8.04) * mm, v(-17.68, 8.04) * mm, v(-17.65, 8.03) * mm, v(-17.62, 8.03) * mm, v(-17.6, 8.02) * mm, v(-17.61, 8.01) * mm], "startDerivative": vector(0, -0.1) * mm, "endDerivative": vector(-0.17, -0.09) * mm});
            skFitSpline(sketch, "E187", {"points": [v(-17.56, 8) * mm, v(-17.56, 8) * mm, v(-17.56, 8) * mm, v(-17.56, 8.01) * mm, v(-17.57, 8.02) * mm, v(-17.57, 8.03) * mm, v(-17.56, 8.04) * mm, v(-17.54, 8.04) * mm, v(-17.52, 8.04) * mm, v(-17.5, 8.04) * mm, v(-17.5, 8.05) * mm], "startDerivative": vector(-0.05, 0) * mm, "endDerivative": vector(-0.08, 0.11) * mm});
            skFitSpline(sketch, "E188", {"points": [v(-17.4, 8.06) * mm, v(-17.4, 8.04) * mm, v(-17.35, 8.04) * mm, v(-17.34, 8.03) * mm, v(-17.33, 8.03) * mm, v(-17.32, 8.02) * mm, v(-17.33, 8) * mm], "startDerivative": vector(0, -0.11) * mm, "endDerivative": vector(-0.07, -0.1) * mm});
            skFitSpline(sketch, "E189", {"points": [v(-17.55, 8.5) * mm, v(-17.57, 8.48) * mm, v(-17.57, 8.46) * mm, v(-17.5, 8.46) * mm, v(-17.5, 8.46) * mm, v(-17.52, 8.44) * mm], "startDerivative": vector(-0.1, -0.03) * mm, "endDerivative": vector(-0.12, -0.1) * mm});
            skFitSpline(sketch, "E190", {"points": [v(-17.44, 8.45) * mm, v(-17.42, 8.47) * mm, v(-17.36, 8.47) * mm, v(-17.35, 8.47) * mm, v(-17.34, 8.48) * mm, v(-17.34, 8.5) * mm, v(-17.35, 8.5) * mm], "startDerivative": vector(0.05, 0.09) * mm, "endDerivative": vector(-0.1, -0.02) * mm});
            skSolve(sketch);
        }
        {
            var Q0;
            Q0 = qSketchRegion(id + "F2", true);
            extrude(context, id + "F3", {"entities" : qUnion([Q0]), "operationType" : NewBodyOperationType.ADD, "depth" : 0.5 * mm, "offsetDistance" : 25.4 * mm});
        }
        {
            var Q0;
            Q0=makeQuery(id+"F3.boolean.opBoolean","SPLIT",FACE,{"disambiguationData":[TD([makeQuery(id+"F3.opExtrude","SWEPT_FACE",FACE,{"disambiguationData":[OSD([sQuery(id+"F2.wireOp",EDGE,"E76")])]})])],"derivedFrom":makeQuery(id+"F1.opExtrude","CAP_FACE",FACE,{"disambiguationData":[OSD([sQuery(id+"F0.wireOp",EDGE,"E0.bottom"),sQuery(id+"F0.wireOp",EDGE,"E0.top"),sQuery(id+"F0.wireOp",EDGE,"E0.left"),sQuery(id+"F0.wireOp",EDGE,"E0.right"),sQuery(id+"F0.wireOp",EDGE,"E1.filletArc"),sQuery(id+"F0.wireOp",EDGE,"E2.filletArc"),sQuery(id+"F0.wireOp",EDGE,"E3.filletArc"),sQuery(id+"F0.wireOp",EDGE,"E4.filletArc"),sQuery(id+"F0.wireOp",EDGE,"E5")])],"isStart":false})});
            extrude(context, id + "F4", {"entities" : qUnion([Q0]), "operationType" : NewBodyOperationType.ADD, "depth" : 0.76 * mm, "offsetDistance" : 25.4 * mm});
        }
        {
            var Q0;
            Q0=makeQuery(id+"F4.opExtrude","CAP_FACE",FACE,{"disambiguationData":[OSD([sQuery(id+"F0.wireOp",EDGE,"E0.bottom"),sQuery(id+"F0.wireOp",EDGE,"E0.top"),sQuery(id+"F0.wireOp",EDGE,"E0.left"),sQuery(id+"F0.wireOp",EDGE,"E0.right"),sQuery(id+"F0.wireOp",EDGE,"E1.filletArc"),sQuery(id+"F0.wireOp",EDGE,"E2.filletArc"),sQuery(id+"F0.wireOp",EDGE,"E3.filletArc"),sQuery(id+"F0.wireOp",EDGE,"E4.filletArc"),sQuery(id+"F0.wireOp",EDGE,"E5")])],"isStart":false});
            var sketch = newSketch(context, id + "F5", { "sketchPlane" : qUnion([Q0])});
            skLineSegment(sketch, "E191", {"start": v(-9.6, 11.23) * mm, "end": v(-9.6, 12.38) * mm});
            skLineSegment(sketch, "E192", {"start": v(-9.6, 12.38) * mm, "end": v(-9.08, 12.38) * mm});
            skLineSegment(sketch, "E193", {"start": v(-9.08, 12.28) * mm, "end": v(-9.48, 12.28) * mm});
            skLineSegment(sketch, "E194", {"start": v(-9.48, 12.28) * mm, "end": v(-9.48, 11.9) * mm});
            skLineSegment(sketch, "E195", {"start": v(-9.48, 11.9) * mm, "end": v(-9.07, 11.9) * mm});
            skLineSegment(sketch, "E196", {"start": v(-9.48, 11.22) * mm, "end": v(-9.48, 11.8) * mm});
            skLineSegment(sketch, "E197", {"start": v(-9.48, 11.8) * mm, "end": v(-9.06, 11.8) * mm});
            skArc(sketch, "E198", {"start": v(-9.07, 11.9) * mm, "mid": v(-8.91, 12.1) * mm, "end": v(-9.08, 12.28) * mm});
            skArc(sketch, "E199", {"start": v(-9.06, 11.8) * mm, "mid": v(-8.8, 12.1) * mm, "end": v(-9.08, 12.38) * mm});
            skArc(sketch, "E200", {"start": v(-9.6, 11.23) * mm, "mid": v(-9.54, 11.17) * mm, "end": v(-9.48, 11.22) * mm});
            skCircle(sketch, "E201", {"center": v(-8.54, 12.3) * mm, "radius": 0.07 * mm});
            skLineSegment(sketch, "E202", {"start": v(-8.6, 12.04) * mm, "end": v(-8.6, 11.23) * mm});
            skLineSegment(sketch, "E203", {"start": v(-8.5, 12.04) * mm, "end": v(-8.5, 11.23) * mm});
            skArc(sketch, "E204", {"start": v(-8.5, 12.04) * mm, "mid": v(-8.55, 12.1) * mm, "end": v(-8.6, 12.04) * mm});
            skArc(sketch, "E205", {"start": v(-8.6, 11.23) * mm, "mid": v(-8.55, 11.18) * mm, "end": v(-8.5, 11.23) * mm});
            skLineSegment(sketch, "E206", {"start": v(-8.13, 12.06) * mm, "end": v(-7.46, 12.06) * mm});
            skLineSegment(sketch, "E207", {"start": v(-7.46, 12.06) * mm, "end": v(-7.46, 11.92) * mm});
            skLineSegment(sketch, "E208", {"start": v(-7.46, 11.92) * mm, "end": v(-8.12, 11.28) * mm});
            skLineSegment(sketch, "E209", {"start": v(-8.12, 11.28) * mm, "end": v(-7.56, 11.28) * mm});
            skLineSegment(sketch, "E210", {"start": v(-7.56, 11.28) * mm, "end": v(-7.52, 11.33) * mm});
            skLineSegment(sketch, "E211", {"start": v(-7.52, 11.33) * mm, "end": v(-7.52, 11.46) * mm});
            skLineSegment(sketch, "E212", {"start": v(-8.1, 11.95) * mm, "end": v(-7.58, 11.95) * mm});
            skLineSegment(sketch, "E213", {"start": v(-7.58, 11.95) * mm, "end": v(-8.24, 11.32) * mm});
            skLineSegment(sketch, "E214", {"start": v(-8.24, 11.32) * mm, "end": v(-8.24, 11.18) * mm});
            skLineSegment(sketch, "E215", {"start": v(-8.24, 11.18) * mm, "end": v(-7.54, 11.18) * mm});
            skFitSpline(sketch, "E216", {"points": [v(-8.13, 12.06) * mm, v(-8.17, 12.04) * mm, v(-8.21, 12) * mm, v(-8.24, 11.94) * mm, v(-8.24, 11.89) * mm, v(-8.24, 11.81) * mm, v(-8.24, 11.78) * mm, v(-8.23, 11.76) * mm, v(-8.2, 11.75) * mm, v(-8.17, 11.75) * mm, v(-8.15, 11.78) * mm, v(-8.14, 11.83) * mm, v(-8.14, 11.88) * mm, v(-8.14, 11.9) * mm, v(-8.13, 11.93) * mm, v(-8.1, 11.95) * mm], "startDerivative": vector(-0.6, -0.2) * mm, "endDerivative": vector(0.56, 0.28) * mm});
            skPoint(sketch, "E217.5.internal.snap0", {"position": v(-7.52, 11.4) * mm});
            skFitSpline(sketch, "E217", {"points": [v(-7.54, 11.18) * mm, v(-7.52, 11.18) * mm, v(-7.48, 11.2) * mm, v(-7.44, 11.26) * mm, v(-7.42, 11.32) * mm, v(-7.42, 11.4) * mm, v(-7.42, 11.46) * mm, v(-7.43, 11.48) * mm, v(-7.44, 11.48) * mm, v(-7.46, 11.48) * mm, v(-7.48, 11.48) * mm, v(-7.5, 11.48) * mm, v(-7.52, 11.46) * mm], "startDerivative": vector(0.33, -0.05) * mm, "endDerivative": vector(-0.16, -0.31) * mm});
            skLineSegment(sketch, "E218", {"start": v(-7.08, 12.06) * mm, "end": v(-6.41, 12.06) * mm});
            skLineSegment(sketch, "E219", {"start": v(-6.41, 12.06) * mm, "end": v(-6.41, 11.92) * mm});
            skLineSegment(sketch, "E220", {"start": v(-6.41, 11.92) * mm, "end": v(-7.06, 11.29) * mm});
            skLineSegment(sketch, "E221", {"start": v(-7.06, 11.29) * mm, "end": v(-6.5, 11.29) * mm});
            skLineSegment(sketch, "E222", {"start": v(-6.5, 11.29) * mm, "end": v(-6.46, 11.33) * mm});
            skLineSegment(sketch, "E223", {"start": v(-6.46, 11.33) * mm, "end": v(-6.46, 11.46) * mm});
            skLineSegment(sketch, "E224", {"start": v(-7.05, 11.95) * mm, "end": v(-6.52, 11.95) * mm});
            skLineSegment(sketch, "E225", {"start": v(-6.52, 11.95) * mm, "end": v(-7.19, 11.32) * mm});
            skLineSegment(sketch, "E226", {"start": v(-7.19, 11.32) * mm, "end": v(-7.19, 11.18) * mm});
            skLineSegment(sketch, "E227", {"start": v(-7.19, 11.18) * mm, "end": v(-6.49, 11.18) * mm});
            skFitSpline(sketch, "E228", {"points": [v(-7.08, 12.06) * mm, v(-7.12, 12.04) * mm, v(-7.16, 12) * mm, v(-7.2, 11.94) * mm, v(-7.2, 11.89) * mm, v(-7.2, 11.81) * mm, v(-7.2, 11.78) * mm, v(-7.18, 11.76) * mm, v(-7.15, 11.76) * mm, v(-7.11, 11.76) * mm, v(-7.1, 11.78) * mm, v(-7.1, 11.83) * mm, v(-7.1, 11.88) * mm, v(-7.1, 11.9) * mm, v(-7.08, 11.93) * mm, v(-7.05, 11.95) * mm], "startDerivative": vector(-0.6, -0.2) * mm, "endDerivative": vector(0.56, 0.28) * mm});
            skPoint(sketch, "E229.5.internal.snap0", {"position": v(-6.46, 11.4) * mm});
            skFitSpline(sketch, "E229", {"points": [v(-6.49, 11.18) * mm, v(-6.46, 11.18) * mm, v(-6.43, 11.2) * mm, v(-6.39, 11.26) * mm, v(-6.37, 11.32) * mm, v(-6.37, 11.4) * mm, v(-6.37, 11.46) * mm, v(-6.38, 11.48) * mm, v(-6.39, 11.48) * mm, v(-6.4, 11.48) * mm, v(-6.43, 11.48) * mm, v(-6.45, 11.48) * mm, v(-6.46, 11.46) * mm], "startDerivative": vector(0.33, -0.05) * mm, "endDerivative": vector(-0.16, -0.31) * mm});
            skLineSegment(sketch, "E230", {"start": v(-9.57, 9.23) * mm, "end": v(-9.57, 10.38) * mm});
            skLineSegment(sketch, "E231", {"start": v(-9.57, 10.38) * mm, "end": v(-9.06, 10.38) * mm});
            skLineSegment(sketch, "E232", {"start": v(-9.05, 10.28) * mm, "end": v(-9.45, 10.28) * mm});
            skLineSegment(sketch, "E233", {"start": v(-9.45, 10.28) * mm, "end": v(-9.45, 9.9) * mm});
            skLineSegment(sketch, "E234", {"start": v(-9.45, 9.9) * mm, "end": v(-9.04, 9.9) * mm});
            skLineSegment(sketch, "E235", {"start": v(-9.45, 9.28) * mm, "end": v(-9.45, 9.8) * mm});
            skLineSegment(sketch, "E236", {"start": v(-9.45, 9.8) * mm, "end": v(-9.04, 9.8) * mm});
            skArc(sketch, "E237", {"start": v(-9.04, 9.9) * mm, "mid": v(-8.89, 10.1) * mm, "end": v(-9.05, 10.28) * mm});
            skArc(sketch, "E238", {"start": v(-8.87, 9.86) * mm, "mid": v(-8.78, 10.19) * mm, "end": v(-9.06, 10.38) * mm});
            skArc(sketch, "E239", {"start": v(-8.94, 9.18) * mm, "mid": v(-8.71, 9.5) * mm, "end": v(-8.87, 9.86) * mm});
            skArc(sketch, "E240", {"start": v(-8.83, 9.69) * mm, "mid": v(-8.92, 9.76) * mm, "end": v(-9.04, 9.8) * mm});
            skLineSegment(sketch, "E241", {"start": v(-8.83, 9.69) * mm, "end": v(-8.83, 9.41) * mm});
            skArc(sketch, "E242", {"start": v(-8.95, 9.28) * mm, "mid": v(-8.87, 9.32) * mm, "end": v(-8.83, 9.41) * mm});
            skLineSegment(sketch, "E243", {"start": v(-8.95, 9.28) * mm, "end": v(-9.45, 9.28) * mm});
            skLineSegment(sketch, "E244", {"start": v(-9.57, 9.23) * mm, "end": v(-9.57, 9.17) * mm});
            skLineSegment(sketch, "E245", {"start": v(-9.57, 9.17) * mm, "end": v(-8.94, 9.18) * mm});
            skLineSegment(sketch, "E246", {"start": v(-9.56, 7.22) * mm, "end": v(-9.56, 8.37) * mm});
            skLineSegment(sketch, "E247", {"start": v(-9.56, 8.37) * mm, "end": v(-9.05, 8.37) * mm});
            skLineSegment(sketch, "E248", {"start": v(-9.04, 8.28) * mm, "end": v(-9.44, 8.28) * mm});
            skLineSegment(sketch, "E249", {"start": v(-9.44, 8.28) * mm, "end": v(-9.44, 7.9) * mm});
            skLineSegment(sketch, "E250", {"start": v(-9.44, 7.9) * mm, "end": v(-9.03, 7.9) * mm});
            skLineSegment(sketch, "E251", {"start": v(-9.44, 7.28) * mm, "end": v(-9.44, 7.8) * mm});
            skLineSegment(sketch, "E252", {"start": v(-9.44, 7.8) * mm, "end": v(-9.02, 7.8) * mm});
            skArc(sketch, "E253", {"start": v(-9.03, 7.9) * mm, "mid": v(-8.88, 8.1) * mm, "end": v(-9.04, 8.28) * mm});
            skArc(sketch, "E254", {"start": v(-8.86, 7.86) * mm, "mid": v(-8.77, 8.18) * mm, "end": v(-9.05, 8.37) * mm});
            skArc(sketch, "E255", {"start": v(-8.93, 7.18) * mm, "mid": v(-8.7, 7.5) * mm, "end": v(-8.86, 7.86) * mm});
            skArc(sketch, "E256", {"start": v(-8.82, 7.68) * mm, "mid": v(-8.9, 7.76) * mm, "end": v(-9.02, 7.8) * mm});
            skLineSegment(sketch, "E257", {"start": v(-8.82, 7.68) * mm, "end": v(-8.82, 7.4) * mm});
            skArc(sketch, "E258", {"start": v(-8.94, 7.28) * mm, "mid": v(-8.86, 7.32) * mm, "end": v(-8.82, 7.4) * mm});
            skLineSegment(sketch, "E259", {"start": v(-8.94, 7.28) * mm, "end": v(-9.44, 7.28) * mm});
            skLineSegment(sketch, "E260", {"start": v(-9.56, 7.22) * mm, "end": v(-9.56, 7.17) * mm});
            skLineSegment(sketch, "E261", {"start": v(-9.56, 7.17) * mm, "end": v(-8.93, 7.18) * mm});
            skLineSegment(sketch, "E262", {"start": v(-5.97, 12.06) * mm, "end": v(-5.51, 12.06) * mm});
            skArc(sketch, "E263", {"start": v(-5.39, 11.94) * mm, "mid": v(-5.43, 12.02) * mm, "end": v(-5.51, 12.06) * mm});
            skLineSegment(sketch, "E264", {"start": v(-5.39, 11.94) * mm, "end": v(-5.39, 11.2) * mm});
            skArc(sketch, "E265", {"start": v(-5.45, 11.2) * mm, "mid": v(-5.42, 11.17) * mm, "end": v(-5.39, 11.2) * mm});
            skLineSegment(sketch, "E266", {"start": v(-5.45, 11.2) * mm, "end": v(-5.45, 11.33) * mm});
            skArc(sketch, "E267", {"start": v(-5.67, 11.2) * mm, "mid": v(-5.55, 11.24) * mm, "end": v(-5.45, 11.33) * mm});
            skLineSegment(sketch, "E268", {"start": v(-5.67, 11.2) * mm, "end": v(-6.04, 11.2) * mm});
            skArc(sketch, "E269", {"start": v(-6.16, 11.33) * mm, "mid": v(-6.1, 11.25) * mm, "end": v(-6.04, 11.2) * mm});
            skLineSegment(sketch, "E270", {"start": v(-6.16, 11.33) * mm, "end": v(-6.16, 11.5) * mm});
            skArc(sketch, "E271", {"start": v(-5.92, 11.73) * mm, "mid": v(-6.09, 11.67) * mm, "end": v(-6.16, 11.5) * mm});
            skLineSegment(sketch, "E272", {"start": v(-5.92, 11.73) * mm, "end": v(-5.48, 11.73) * mm});
            skLineSegment(sketch, "E273", {"start": v(-5.48, 11.73) * mm, "end": v(-5.48, 11.9) * mm});
            skLineSegment(sketch, "E274", {"start": v(-5.48, 11.9) * mm, "end": v(-5.51, 11.95) * mm});
            skLineSegment(sketch, "E275", {"start": v(-5.51, 11.95) * mm, "end": v(-5.96, 11.95) * mm});
            skArc(sketch, "E276", {"start": v(-5.96, 11.95) * mm, "mid": v(-6.02, 11.93) * mm, "end": v(-6.06, 11.88) * mm});
            skLineSegment(sketch, "E277", {"start": v(-6.06, 11.88) * mm, "end": v(-6.06, 11.8) * mm});
            skArc(sketch, "E278", {"start": v(-6.17, 11.8) * mm, "mid": v(-6.11, 11.77) * mm, "end": v(-6.06, 11.8) * mm});
            skLineSegment(sketch, "E279", {"start": v(-6.17, 11.8) * mm, "end": v(-6.17, 11.92) * mm});
            skArc(sketch, "E280", {"start": v(-5.97, 12.06) * mm, "mid": v(-6.09, 12.02) * mm, "end": v(-6.17, 11.92) * mm});
            skLineSegment(sketch, "E281", {"start": v(-5.88, 11.65) * mm, "end": v(-5.48, 11.65) * mm});
            skLineSegment(sketch, "E282", {"start": v(-5.48, 11.65) * mm, "end": v(-5.48, 11.51) * mm});
            skLineSegment(sketch, "E283", {"start": v(-6.06, 11.52) * mm, "end": v(-6.06, 11.36) * mm});
            skLineSegment(sketch, "E284", {"start": v(-6, 11.3) * mm, "end": v(-5.7, 11.3) * mm});
            skArc(sketch, "E285", {"start": v(-5.88, 11.65) * mm, "mid": v(-6, 11.61) * mm, "end": v(-6.06, 11.52) * mm});
            skArc(sketch, "E286", {"start": v(-6.06, 11.36) * mm, "mid": v(-6.04, 11.31) * mm, "end": v(-6, 11.3) * mm});
            skArc(sketch, "E287", {"start": v(-5.7, 11.3) * mm, "mid": v(-5.54, 11.36) * mm, "end": v(-5.48, 11.51) * mm});
            skLineSegment(sketch, "E288", {"start": v(-8.3, 10.04) * mm, "end": v(-7.85, 10.04) * mm});
            skArc(sketch, "E289", {"start": v(-7.72, 9.92) * mm, "mid": v(-7.76, 10) * mm, "end": v(-7.85, 10.04) * mm});
            skLineSegment(sketch, "E290", {"start": v(-7.72, 9.92) * mm, "end": v(-7.72, 9.2) * mm});
            skArc(sketch, "E291", {"start": v(-7.79, 9.2) * mm, "mid": v(-7.75, 9.16) * mm, "end": v(-7.72, 9.2) * mm});
            skLineSegment(sketch, "E292", {"start": v(-7.79, 9.2) * mm, "end": v(-7.79, 9.31) * mm});
            skArc(sketch, "E293", {"start": v(-8, 9.18) * mm, "mid": v(-7.88, 9.22) * mm, "end": v(-7.79, 9.31) * mm});
            skLineSegment(sketch, "E294", {"start": v(-8, 9.18) * mm, "end": v(-8.37, 9.18) * mm});
            skArc(sketch, "E295", {"start": v(-8.5, 9.31) * mm, "mid": v(-8.44, 9.23) * mm, "end": v(-8.37, 9.18) * mm});
            skLineSegment(sketch, "E296", {"start": v(-8.5, 9.31) * mm, "end": v(-8.5, 9.5) * mm});
            skArc(sketch, "E297", {"start": v(-8.26, 9.71) * mm, "mid": v(-8.42, 9.65) * mm, "end": v(-8.5, 9.5) * mm});
            skLineSegment(sketch, "E298", {"start": v(-8.26, 9.71) * mm, "end": v(-7.81, 9.71) * mm});
            skLineSegment(sketch, "E299", {"start": v(-7.81, 9.71) * mm, "end": v(-7.81, 9.89) * mm});
            skLineSegment(sketch, "E300", {"start": v(-7.81, 9.89) * mm, "end": v(-7.85, 9.93) * mm});
            skLineSegment(sketch, "E301", {"start": v(-7.85, 9.93) * mm, "end": v(-8.3, 9.93) * mm});
            skArc(sketch, "E302", {"start": v(-8.3, 9.93) * mm, "mid": v(-8.36, 9.91) * mm, "end": v(-8.4, 9.87) * mm});
            skLineSegment(sketch, "E303", {"start": v(-8.4, 9.87) * mm, "end": v(-8.4, 9.79) * mm});
            skArc(sketch, "E304", {"start": v(-8.5, 9.79) * mm, "mid": v(-8.45, 9.76) * mm, "end": v(-8.4, 9.79) * mm});
            skLineSegment(sketch, "E305", {"start": v(-8.5, 9.79) * mm, "end": v(-8.5, 9.9) * mm});
            skArc(sketch, "E306", {"start": v(-8.3, 10.04) * mm, "mid": v(-8.42, 10) * mm, "end": v(-8.5, 9.9) * mm});
            skLineSegment(sketch, "E307", {"start": v(-8.22, 9.63) * mm, "end": v(-7.81, 9.63) * mm});
            skLineSegment(sketch, "E308", {"start": v(-7.81, 9.63) * mm, "end": v(-7.81, 9.5) * mm});
            skLineSegment(sketch, "E309", {"start": v(-8.4, 9.5) * mm, "end": v(-8.4, 9.35) * mm});
            skLineSegment(sketch, "E310", {"start": v(-8.33, 9.28) * mm, "end": v(-8.02, 9.28) * mm});
            skArc(sketch, "E311", {"start": v(-8.22, 9.63) * mm, "mid": v(-8.33, 9.6) * mm, "end": v(-8.4, 9.5) * mm});
            skArc(sketch, "E312", {"start": v(-8.4, 9.35) * mm, "mid": v(-8.38, 9.3) * mm, "end": v(-8.33, 9.28) * mm});
            skArc(sketch, "E313", {"start": v(-8.02, 9.28) * mm, "mid": v(-7.87, 9.34) * mm, "end": v(-7.81, 9.5) * mm});
            skLineSegment(sketch, "E314", {"start": v(-6.47, 8.05) * mm, "end": v(-6.01, 8.05) * mm});
            skArc(sketch, "E315", {"start": v(-5.89, 7.93) * mm, "mid": v(-5.93, 8.01) * mm, "end": v(-6.01, 8.05) * mm});
            skLineSegment(sketch, "E316", {"start": v(-5.89, 7.93) * mm, "end": v(-5.89, 7.2) * mm});
            skArc(sketch, "E317", {"start": v(-5.95, 7.2) * mm, "mid": v(-5.92, 7.17) * mm, "end": v(-5.89, 7.2) * mm});
            skLineSegment(sketch, "E318", {"start": v(-5.95, 7.2) * mm, "end": v(-5.95, 7.32) * mm});
            skArc(sketch, "E319", {"start": v(-6.17, 7.19) * mm, "mid": v(-6.05, 7.23) * mm, "end": v(-5.95, 7.32) * mm});
            skLineSegment(sketch, "E320", {"start": v(-6.17, 7.19) * mm, "end": v(-6.54, 7.19) * mm});
            skArc(sketch, "E321", {"start": v(-6.66, 7.32) * mm, "mid": v(-6.6, 7.24) * mm, "end": v(-6.54, 7.19) * mm});
            skLineSegment(sketch, "E322", {"start": v(-6.66, 7.32) * mm, "end": v(-6.66, 7.5) * mm});
            skArc(sketch, "E323", {"start": v(-6.42, 7.72) * mm, "mid": v(-6.59, 7.66) * mm, "end": v(-6.66, 7.5) * mm});
            skLineSegment(sketch, "E324", {"start": v(-6.42, 7.72) * mm, "end": v(-5.98, 7.72) * mm});
            skLineSegment(sketch, "E325", {"start": v(-5.98, 7.72) * mm, "end": v(-5.98, 7.9) * mm});
            skLineSegment(sketch, "E326", {"start": v(-5.98, 7.9) * mm, "end": v(-6.01, 7.94) * mm});
            skLineSegment(sketch, "E327", {"start": v(-6.01, 7.94) * mm, "end": v(-6.46, 7.94) * mm});
            skArc(sketch, "E328", {"start": v(-6.46, 7.94) * mm, "mid": v(-6.52, 7.93) * mm, "end": v(-6.56, 7.88) * mm});
            skLineSegment(sketch, "E329", {"start": v(-6.56, 7.88) * mm, "end": v(-6.56, 7.8) * mm});
            skArc(sketch, "E330", {"start": v(-6.67, 7.8) * mm, "mid": v(-6.61, 7.77) * mm, "end": v(-6.56, 7.8) * mm});
            skLineSegment(sketch, "E331", {"start": v(-6.67, 7.8) * mm, "end": v(-6.67, 7.92) * mm});
            skArc(sketch, "E332", {"start": v(-6.47, 8.05) * mm, "mid": v(-6.59, 8.01) * mm, "end": v(-6.67, 7.92) * mm});
            skLineSegment(sketch, "E333", {"start": v(-6.38, 7.64) * mm, "end": v(-5.98, 7.64) * mm});
            skLineSegment(sketch, "E334", {"start": v(-5.98, 7.64) * mm, "end": v(-5.98, 7.5) * mm});
            skLineSegment(sketch, "E335", {"start": v(-6.56, 7.51) * mm, "end": v(-6.56, 7.36) * mm});
            skLineSegment(sketch, "E336", {"start": v(-6.5, 7.29) * mm, "end": v(-6.2, 7.29) * mm});
            skArc(sketch, "E337", {"start": v(-6.38, 7.64) * mm, "mid": v(-6.5, 7.6) * mm, "end": v(-6.56, 7.51) * mm});
            skArc(sketch, "E338", {"start": v(-6.56, 7.36) * mm, "mid": v(-6.54, 7.3) * mm, "end": v(-6.5, 7.29) * mm});
            skArc(sketch, "E339", {"start": v(-6.2, 7.29) * mm, "mid": v(-6.04, 7.35) * mm, "end": v(-5.98, 7.5) * mm});
            skLineSegment(sketch, "E340", {"start": v(-7.43, 10.01) * mm, "end": v(-7.43, 9.21) * mm});
            skLineSegment(sketch, "E341", {"start": v(-7.33, 10.01) * mm, "end": v(-7.33, 9.9) * mm});
            skLineSegment(sketch, "E342", {"start": v(-7.32, 9.21) * mm, "end": v(-7.32, 9.7) * mm});
            skLineSegment(sketch, "E343", {"start": v(-7.1, 9.95) * mm, "end": v(-6.92, 9.95) * mm});
            skLineSegment(sketch, "E344", {"start": v(-7.06, 10.05) * mm, "end": v(-6.93, 10.05) * mm});
            skArc(sketch, "E345", {"start": v(-7.33, 10.01) * mm, "mid": v(-7.38, 10.04) * mm, "end": v(-7.43, 10.01) * mm});
            skArc(sketch, "E346", {"start": v(-6.92, 9.95) * mm, "mid": v(-6.88, 10) * mm, "end": v(-6.93, 10.05) * mm});
            skArc(sketch, "E347", {"start": v(-7.1, 9.95) * mm, "mid": v(-7.25, 9.85) * mm, "end": v(-7.32, 9.7) * mm});
            skArc(sketch, "E348", {"start": v(-7.43, 9.21) * mm, "mid": v(-7.37, 9.16) * mm, "end": v(-7.32, 9.21) * mm});
            skLineSegment(sketch, "E349", {"start": v(-7.5, 8.05) * mm, "end": v(-7.17, 8.05) * mm});
            skLineSegment(sketch, "E350", {"start": v(-7.51, 7.95) * mm, "end": v(-7.16, 7.95) * mm});
            skLineSegment(sketch, "E351", {"start": v(-7.67, 7.74) * mm, "end": v(-6.98, 7.74) * mm});
            skLineSegment(sketch, "E352", {"start": v(-6.98, 7.74) * mm, "end": v(-6.98, 7.8) * mm});
            skLineSegment(sketch, "E353", {"start": v(-7.67, 7.74) * mm, "end": v(-7.67, 7.83) * mm});
            skLineSegment(sketch, "E354", {"start": v(-6.88, 7.8) * mm, "end": v(-6.88, 7.64) * mm});
            skLineSegment(sketch, "E355", {"start": v(-6.88, 7.64) * mm, "end": v(-7.66, 7.64) * mm});
            skLineSegment(sketch, "E356", {"start": v(-7.66, 7.64) * mm, "end": v(-7.66, 7.45) * mm});
            skLineSegment(sketch, "E357", {"start": v(-7.53, 7.29) * mm, "end": v(-7.03, 7.29) * mm});
            skLineSegment(sketch, "E358", {"start": v(-7, 7.31) * mm, "end": v(-7, 7.41) * mm});
            skLineSegment(sketch, "E359", {"start": v(-7.52, 7.18) * mm, "end": v(-7.02, 7.18) * mm});
            skLineSegment(sketch, "E360", {"start": v(-6.9, 7.3) * mm, "end": v(-6.9, 7.41) * mm});
            skLineSegment(sketch, "E361", {"start": v(-7.76, 7.83) * mm, "end": v(-7.76, 7.39) * mm});
            skArc(sketch, "E362", {"start": v(-7.5, 8.05) * mm, "mid": v(-7.67, 7.98) * mm, "end": v(-7.76, 7.83) * mm});
            skArc(sketch, "E363", {"start": v(-6.88, 7.8) * mm, "mid": v(-6.98, 7.97) * mm, "end": v(-7.17, 8.05) * mm});
            skArc(sketch, "E364", {"start": v(-6.98, 7.8) * mm, "mid": v(-7.05, 7.9) * mm, "end": v(-7.16, 7.95) * mm});
            skArc(sketch, "E365", {"start": v(-7.66, 7.45) * mm, "mid": v(-7.62, 7.35) * mm, "end": v(-7.53, 7.29) * mm});
            skArc(sketch, "E366", {"start": v(-7.76, 7.39) * mm, "mid": v(-7.68, 7.24) * mm, "end": v(-7.52, 7.18) * mm});
            skArc(sketch, "E367", {"start": v(-6.9, 7.41) * mm, "mid": v(-6.95, 7.45) * mm, "end": v(-7, 7.41) * mm});
            skLineSegment(sketch, "E368", {"start": v(-4.72, 8.35) * mm, "end": v(-4.72, 7.22) * mm});
            skLineSegment(sketch, "E369", {"start": v(-4.82, 8.35) * mm, "end": v(-4.82, 8.05) * mm});
            skLineSegment(sketch, "E370", {"start": v(-4.82, 8.05) * mm, "end": v(-5.34, 8.05) * mm});
            skLineSegment(sketch, "E371", {"start": v(-5.34, 7.95) * mm, "end": v(-4.82, 7.95) * mm});
            skLineSegment(sketch, "E372", {"start": v(-4.82, 7.95) * mm, "end": v(-4.82, 7.52) * mm});
            skLineSegment(sketch, "E373", {"start": v(-5.5, 7.84) * mm, "end": v(-5.5, 7.41) * mm});
            skLineSegment(sketch, "E374", {"start": v(-5.37, 7.28) * mm, "end": v(-5.04, 7.28) * mm});
            skLineSegment(sketch, "E375", {"start": v(-5.38, 7.18) * mm, "end": v(-5.04, 7.18) * mm});
            skLineSegment(sketch, "E376", {"start": v(-4.82, 7.32) * mm, "end": v(-4.81, 7.21) * mm});
            skArc(sketch, "E377", {"start": v(-5.34, 7.95) * mm, "mid": v(-5.44, 7.92) * mm, "end": v(-5.5, 7.84) * mm});
            skArc(sketch, "E378", {"start": v(-4.72, 8.35) * mm, "mid": v(-4.77, 8.38) * mm, "end": v(-4.82, 8.35) * mm});
            skArc(sketch, "E379", {"start": v(-5.34, 8.05) * mm, "mid": v(-5.5, 8) * mm, "end": v(-5.6, 7.85) * mm});
            skLineSegment(sketch, "E380", {"start": v(-5.6, 7.85) * mm, "end": v(-5.6, 7.37) * mm});
            skArc(sketch, "E381", {"start": v(-5.5, 7.41) * mm, "mid": v(-5.47, 7.32) * mm, "end": v(-5.37, 7.28) * mm});
            skArc(sketch, "E382", {"start": v(-5.6, 7.37) * mm, "mid": v(-5.52, 7.23) * mm, "end": v(-5.38, 7.18) * mm});
            skArc(sketch, "E383", {"start": v(-5.04, 7.28) * mm, "mid": v(-4.88, 7.36) * mm, "end": v(-4.82, 7.52) * mm});
            skArc(sketch, "E384", {"start": v(-5.04, 7.18) * mm, "mid": v(-4.91, 7.22) * mm, "end": v(-4.82, 7.32) * mm});
            skArc(sketch, "E385", {"start": v(-4.81, 7.21) * mm, "mid": v(-4.76, 7.16) * mm, "end": v(-4.72, 7.22) * mm});
            skLineSegment(sketch, "E386", {"start": v(-8.48, 8.03) * mm, "end": v(-8.48, 7.23) * mm});
            skLineSegment(sketch, "E387", {"start": v(-8.38, 8.03) * mm, "end": v(-8.38, 7.92) * mm});
            skLineSegment(sketch, "E388", {"start": v(-8.36, 7.23) * mm, "end": v(-8.36, 7.71) * mm});
            skLineSegment(sketch, "E389", {"start": v(-8.15, 7.96) * mm, "end": v(-7.97, 7.96) * mm});
            skLineSegment(sketch, "E390", {"start": v(-8.1, 8.06) * mm, "end": v(-7.98, 8.06) * mm});
            skArc(sketch, "E391", {"start": v(-8.38, 8.03) * mm, "mid": v(-8.43, 8.06) * mm, "end": v(-8.48, 8.03) * mm});
            skArc(sketch, "E392", {"start": v(-7.97, 7.96) * mm, "mid": v(-7.93, 8.02) * mm, "end": v(-7.98, 8.06) * mm});
            skArc(sketch, "E393", {"start": v(-8.15, 7.96) * mm, "mid": v(-8.3, 7.87) * mm, "end": v(-8.36, 7.71) * mm});
            skArc(sketch, "E394", {"start": v(-8.48, 7.23) * mm, "mid": v(-8.42, 7.18) * mm, "end": v(-8.36, 7.23) * mm});
            skArc(sketch, "E395", {"start": v(-7.06, 10.05) * mm, "mid": v(-7.21, 10) * mm, "end": v(-7.33, 9.9) * mm});
            skArc(sketch, "E396", {"start": v(-8.1, 8.06) * mm, "mid": v(-8.26, 8.02) * mm, "end": v(-8.38, 7.92) * mm});
            skLineSegment(sketch, "E397", {"start": v(-7.03, 7.29) * mm, "end": v(-7, 7.31) * mm});
            skArc(sketch, "E398", {"start": v(-7.02, 7.18) * mm, "mid": v(-6.94, 7.22) * mm, "end": v(-6.9, 7.3) * mm});
            skArc(sketch, "E399", {"start": v(-7.51, 7.95) * mm, "mid": v(-7.61, 7.92) * mm, "end": v(-7.67, 7.83) * mm});
            skSolve(sketch);
        }
        {
            var Q0;
            Q0 = qSketchRegion(id + "F5", true);
            extrude(context, id + "F6", {"entities" : qUnion([Q0]), "operationType" : NewBodyOperationType.REMOVE, "oppositeDirection" : true, "depth" : 0.76 * mm, "offsetDistance" : 25.4 * mm});
        }
        {
            var Q0;
            Q0=makeQuery(id+"F2.imprint","IMPRINT",FACE,{"disambiguationData":[TD([[makeQuery(id+"F2.imprint","IMPRINT",EDGE,{"derivedFrom":sQuery(id+"F2.wireOp",EDGE,"E77")}),-1.0]])]});
            var Q1;
            {var subQ2=sQuery(id+"F2.wireOp",EDGE,"E115");Q1=makeQuery(id+"F2.imprint","IMPRINT",FACE,{"disambiguationData":[TD([[makeQuery(id+"F2.imprint","IMPRINT",EDGE,{"derivedFrom":subQ2}),-1.0]])]});}
            var Q2;
            Q2=makeQuery(id+"F2.imprint","IMPRINT",FACE,{"disambiguationData":[TD([[makeQuery(id+"F2.imprint","IMPRINT",EDGE,{"derivedFrom":sQuery(id+"F2.wireOp",EDGE,"E94")}),-1.0]])]});
            var Q3;
            Q3=makeQuery(id+"F2.imprint","IMPRINT",FACE,{"disambiguationData":[TD([[makeQuery(id+"F2.imprint","IMPRINT",EDGE,{"derivedFrom":sQuery(id+"F2.wireOp",EDGE,"E101")}),1.0]])]});
            var Q4;
            Q4=makeQuery(id+"F2.imprint","IMPRINT",FACE,{"disambiguationData":[TD([[makeQuery(id+"F2.imprint","IMPRINT",EDGE,{"derivedFrom":sQuery(id+"F2.wireOp",EDGE,"E118")}),1.0]])]});
            var Q5;
            Q5=makeQuery(id+"F2.imprint","IMPRINT",FACE,{"disambiguationData":[TD([[makeQuery(id+"F2.imprint","IMPRINT",EDGE,{"derivedFrom":sQuery(id+"F2.wireOp",EDGE,"E123")}),-1.0]])]});
            var Q6;
            Q6=makeQuery(id+"F2.imprint","IMPRINT",FACE,{"disambiguationData":[TD([[makeQuery(id+"F2.imprint","IMPRINT",EDGE,{"derivedFrom":sQuery(id+"F2.wireOp",EDGE,"E145")}),1.0]])]});
            var Q7;
            Q7=makeQuery(id+"F2.imprint","IMPRINT",FACE,{"disambiguationData":[TD([[makeQuery(id+"F2.imprint","IMPRINT",EDGE,{"derivedFrom":sQuery(id+"F2.wireOp",EDGE,"E151")}),1.0]])]});
            var Q8;
            Q8=makeQuery(id+"F2.imprint","IMPRINT",FACE,{"disambiguationData":[TD([[makeQuery(id+"F2.imprint","IMPRINT",EDGE,{"derivedFrom":sQuery(id+"F2.wireOp",EDGE,"E156")}),1.0]])]});
            var Q9;
            Q9=makeQuery(id+"F2.imprint","IMPRINT",FACE,{"disambiguationData":[TD([[makeQuery(id+"F2.imprint","IMPRINT",EDGE,{"derivedFrom":sQuery(id+"F2.wireOp",EDGE,"E160")}),1.0]])]});
            extrude(context, id + "F7", {"entities" : qUnion([Q0, Q1, Q2, Q3, Q4, Q5, Q6, Q7, Q8, Q9]), "operationType" : NewBodyOperationType.ADD, "depth" : 0.25 * mm, "offsetDistance" : 25.4 * mm});
        }
    });
